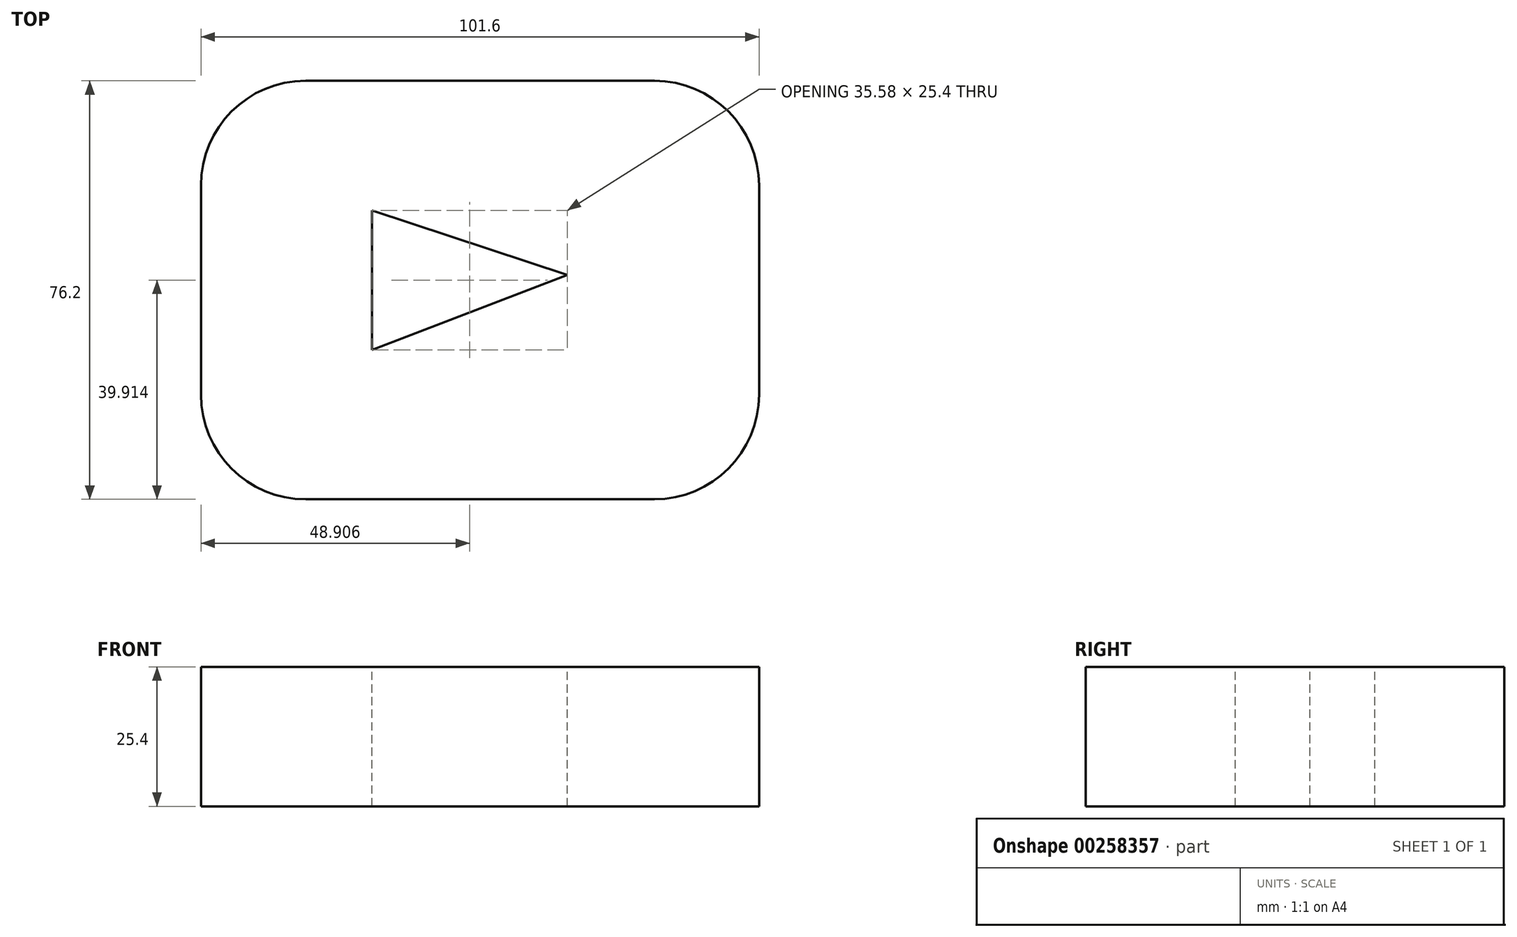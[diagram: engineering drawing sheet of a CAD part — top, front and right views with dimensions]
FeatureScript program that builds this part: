
annotation { "Feature Type Name" : "Feature", "Feature Type Description" : "" }
export const myFeature = defineFeature(function(context is Context, id is Id, definition is map)
    precondition{}
    {
        {
            var Q0;
            Q0=qCreatedBy(makeId("Top.planeOp"),FACE);
            var sketch = newSketch(context, id + "F0", { "sketchPlane" : qUnion([Q0])});
            skLineSegment(sketch, "E0", {"start": v(0, 0) * mm, "end": v(-50.8, 0) * mm});
            skLineSegment(sketch, "E1", {"start": v(-50.8, 0) * mm, "end": v(-50.8, 76.2) * mm});
            skLineSegment(sketch, "E2", {"start": v(-50.8, 76.2) * mm, "end": v(50.8, 76.2) * mm});
            skLineSegment(sketch, "E3", {"start": v(50.8, 76.2) * mm, "end": v(50.8, 0) * mm});
            skLineSegment(sketch, "E4", {"start": v(50.8, 0) * mm, "end": v(0, 0) * mm});
            skSolve(sketch);
        }
        {
            var Q0;
            Q0=makeQuery(id+"F0.imprint","IMPRINT",FACE,{"disambiguationData":[TD([[makeQuery(id+"F0.imprint","IMPRINT",EDGE,{"derivedFrom":sQuery(id+"F0.wireOp",EDGE,"E0")}),-1.0]])]});
            extrude(context, id + "F1", {"entities" : qUnion([Q0]), "depth" : 25.4 * mm});
        }
        {
            var Q0;
            Q0=makeQuery(id+"F1.opExtrude","SWEPT_EDGE",EDGE,{"disambiguationData":[OSD([sQuery(id+"F0.wireOp",EDGE,"E0"),sQuery(id+"F0.wireOp",EDGE,"E1")])]});
            var Q1;
            Q1=makeQuery(id+"F1.opExtrude","SWEPT_EDGE",EDGE,{"disambiguationData":[OSD([sQuery(id+"F0.wireOp",EDGE,"E3"),sQuery(id+"F0.wireOp",EDGE,"E4")])]});
            var Q2;
            Q2=makeQuery(id+"F1.opExtrude","SWEPT_EDGE",EDGE,{"disambiguationData":[OSD([sQuery(id+"F0.wireOp",EDGE,"E1"),sQuery(id+"F0.wireOp",EDGE,"E2")])]});
            var Q3;
            Q3=makeQuery(id+"F1.opExtrude","SWEPT_EDGE",EDGE,{"disambiguationData":[OSD([sQuery(id+"F0.wireOp",EDGE,"E2"),sQuery(id+"F0.wireOp",EDGE,"E3")])]});
            fillet(context, id + "F2", {"entities" : qUnion([Q0, Q1, Q2, Q3]), "radius" : 19.05 * mm, "tangentPropagation" : true, "allowEdgeOverflow" : false});
        }
        {
            var Q0;
            Q0=makeQuery(id+"F1.opExtrude","CAP_FACE",FACE,{"disambiguationData":[OSD([sQuery(id+"F0.wireOp",EDGE,"E0"),sQuery(id+"F0.wireOp",EDGE,"E1"),sQuery(id+"F0.wireOp",EDGE,"E2"),sQuery(id+"F0.wireOp",EDGE,"E3"),sQuery(id+"F0.wireOp",EDGE,"E4")])],"isStart":false});
            var sketch = newSketch(context, id + "F3", { "sketchPlane" : qUnion([Q0])});
            skLineSegment(sketch, "E5", {"start": v(-19.68, 27.21) * mm, "end": v(-19.68, 52.61) * mm});
            skLineSegment(sketch, "E6", {"start": v(-19.68, 52.61) * mm, "end": v(15.9, 40.84) * mm});
            skLineSegment(sketch, "E7", {"start": v(15.9, 40.84) * mm, "end": v(-19.68, 27.21) * mm});
            skSolve(sketch);
        }
        {
            var Q0;
            Q0 = qSketchRegion(id + "F3", true);
            extrude(context, id + "F4", {"entities" : qUnion([Q0]), "operationType" : NewBodyOperationType.REMOVE, "oppositeDirection" : true, "depth" : 254 * mm});
        }
    });
